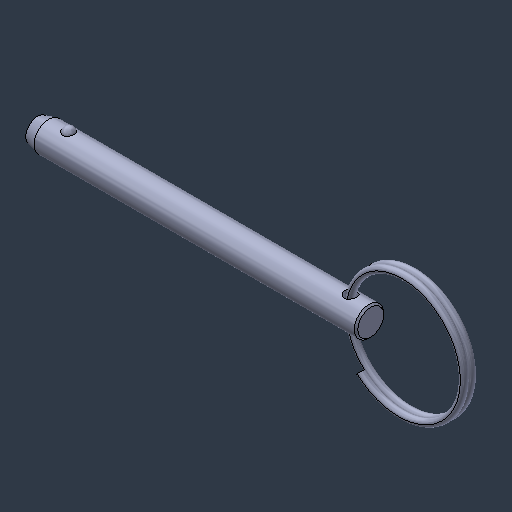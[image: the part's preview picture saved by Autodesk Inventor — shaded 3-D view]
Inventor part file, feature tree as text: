
AUTODESK INVENTOR PART (.ipt)
format: ipt  version: 2024.3 (Build 283343000, 343)  size: 223,744 bytes
history: native  units: mm (DEFAULTED — no unit token found)
features: revolve x1, other x1, sweep x1
ambient origin geometry x8: Origin, YZ Plane, XZ Plane, XY Plane, X Axis, Y Axis, Z Axis, Center Point
bodies: Solid1 (feature_tree), Solid2 (feature_tree), Solid3 (feature_tree)
feature tree (3):
  revolve  "Revolve2"  [1 undecoded]
  other  "Cut-Revolve2"
  sweep  "Sweep2"
note: 1 required parameter value undecoded (feature->parameter linkage not recoverable at this tier; creation-order binding heuristic only, values carry confidence <= 0.55)
